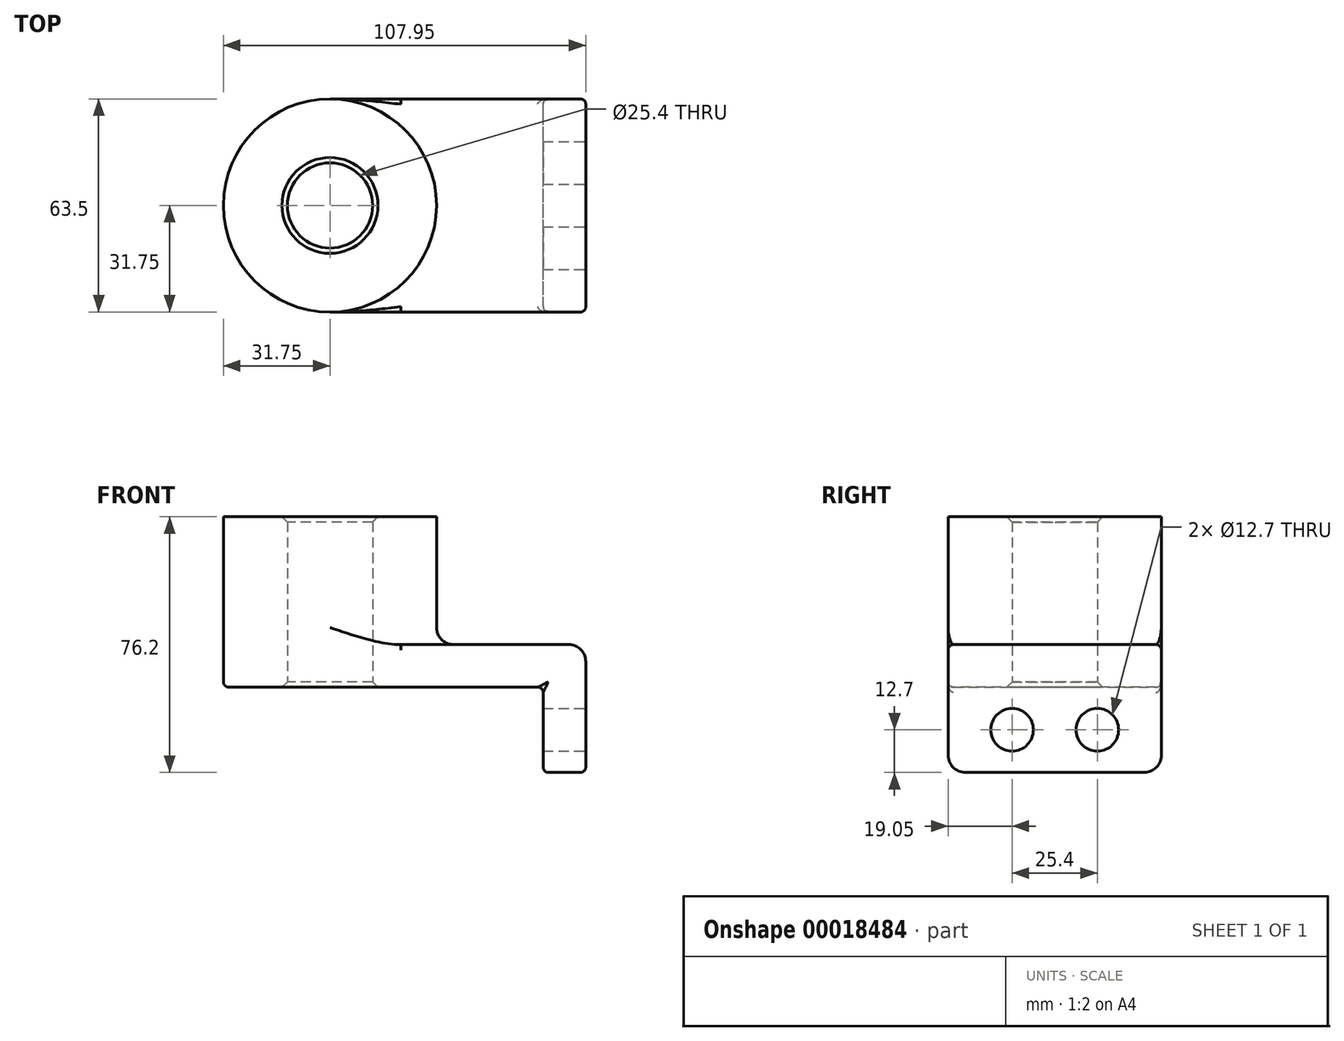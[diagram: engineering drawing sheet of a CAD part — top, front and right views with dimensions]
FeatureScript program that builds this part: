
annotation { "Feature Type Name" : "Feature", "Feature Type Description" : "" }
export const myFeature = defineFeature(function(context is Context, id is Id, definition is map)
    precondition{}
    {
        {
            var Q0;
            Q0=qCreatedBy(makeId("Top.planeOp"),FACE);
            var sketch = newSketch(context, id + "F0", { "sketchPlane" : qUnion([Q0])});
            skLineSegment(sketch, "E0.rect.bottom", {"start": v(38.1, 31.75) * mm, "end": v(-38.1, 31.75) * mm});
            skLineSegment(sketch, "E0.rect.top", {"start": v(38.1, -31.75) * mm, "end": v(-38.1, -31.75) * mm});
            skLineSegment(sketch, "E0.rect.left", {"start": v(38.1, 31.75) * mm, "end": v(38.1, -31.75) * mm});
            skLineSegment(sketch, "E0.rect.right", {"start": v(-38.1, 31.75) * mm, "end": v(-38.1, -31.75) * mm});
            skPoint(sketch, "E0.rect.middle", {"position": v(0, 0) * mm});
            skCircle(sketch, "E1", {"center": v(-38.1, 0) * mm, "radius": 31.75 * mm});
            skCircle(sketch, "E2", {"center": v(-38.1, 0) * mm, "radius": 12.7 * mm});
            skSolve(sketch);
        }
        {
            var Q0;
            {var subQ0=sQuery(id+"F0.wireOp",EDGE,"E2");var subQ1=sQuery(id+"F0.wireOp",EDGE,"E0.rect.right");var subQ3=makeQuery(id+"F0.imprint","INTERSECT",VERTEX,{"disambiguationData":[OD(0.0)],"derivedFrom":[subQ1,subQ0]});Q0=makeQuery(id+"F0.imprint","IMPRINT",FACE,{"disambiguationData":[TD([[makeQuery(id+"F0.imprint","IMPRINT",EDGE,{"disambiguationData":[TD([[subQ3,-1.0]])],"derivedFrom":subQ0}),-1.0]])]});}
            var Q1;
            {var subQ0=sQuery(id+"F0.wireOp",EDGE,"E2");var subQ1=sQuery(id+"F0.wireOp",EDGE,"E0.rect.right");var subQ3=makeQuery(id+"F0.imprint","INTERSECT",VERTEX,{"disambiguationData":[OD(0.0)],"derivedFrom":[subQ1,subQ0]});Q1=makeQuery(id+"F0.imprint","IMPRINT",FACE,{"disambiguationData":[TD([[makeQuery(id+"F0.imprint","IMPRINT",EDGE,{"disambiguationData":[TD([[subQ3,1.0]])],"derivedFrom":subQ0}),-1.0]])]});}
            var Q2;
            {var subQ3=sQuery(id+"F0.wireOp",EDGE,"E0.rect.bottom");Q2=makeQuery(id+"F0.imprint","IMPRINT",FACE,{"disambiguationData":[TD([[makeQuery(id+"F0.imprint","IMPRINT",EDGE,{"derivedFrom":subQ3}),1.0]])]});}
            extrude(context, id + "F1", {"entities" : qUnion([Q0, Q1, Q2]), "depth" : 12.7 * mm});
        }
        {
            var Q0;
            {var subQ0=sQuery(id+"F0.wireOp",EDGE,"E2");var subQ1=sQuery(id+"F0.wireOp",EDGE,"E0.rect.right");var subQ3=makeQuery(id+"F0.imprint","INTERSECT",VERTEX,{"disambiguationData":[OD(0.0)],"derivedFrom":[subQ1,subQ0]});Q0=makeQuery(id+"F0.imprint","IMPRINT",FACE,{"disambiguationData":[TD([[makeQuery(id+"F0.imprint","IMPRINT",EDGE,{"disambiguationData":[TD([[subQ3,-1.0]])],"derivedFrom":subQ0}),-1.0]])]});}
            var Q1;
            {var subQ0=sQuery(id+"F0.wireOp",EDGE,"E2");var subQ1=sQuery(id+"F0.wireOp",EDGE,"E0.rect.right");var subQ3=makeQuery(id+"F0.imprint","INTERSECT",VERTEX,{"disambiguationData":[OD(0.0)],"derivedFrom":[subQ1,subQ0]});Q1=makeQuery(id+"F0.imprint","IMPRINT",FACE,{"disambiguationData":[TD([[makeQuery(id+"F0.imprint","IMPRINT",EDGE,{"disambiguationData":[TD([[subQ3,1.0]])],"derivedFrom":subQ0}),-1.0]])]});}
            extrude(context, id + "F2", {"entities" : qUnion([Q0, Q1]), "flatOperationType" : FlatOperationType.REMOVE, "offsetDistance" : 25.4 * mm, "depth" : 50.8 * mm, "domain" : OperationDomain.MODEL});
        }
        {
            var Q0;
            Q0=makeQuery(id+"F1.opExtrude","SWEPT_FACE",FACE,{"disambiguationData":[OSD([sQuery(id+"F0.wireOp",EDGE,"E0.rect.left")])]});
            var sketch = newSketch(context, id + "F3", { "sketchPlane" : qUnion([Q0])});
            skLineSegment(sketch, "E3.bottom", {"start": v(-31.75, 12.7) * mm, "end": v(31.75, 12.7) * mm});
            skLineSegment(sketch, "E3.top", {"start": v(-31.75, -25.4) * mm, "end": v(31.75, -25.4) * mm});
            skLineSegment(sketch, "E3.left", {"start": v(-31.75, 12.7) * mm, "end": v(-31.75, -25.4) * mm});
            skLineSegment(sketch, "E3.right", {"start": v(31.75, 12.7) * mm, "end": v(31.75, -25.4) * mm});
            skCircle(sketch, "E4", {"center": v(-12.7, -12.7) * mm, "radius": 6.35 * mm});
            skLineSegment(sketch, "E5", {"start": v(0, 0) * mm, "end": v(0, -25.4) * mm});
            skCircle(sketch, "E6.MirrorC", {"center": v(12.7, -12.7) * mm, "radius": 6.35 * mm});
            skSolve(sketch);
        }
        {
            var Q0;
            Q0 = qSketchRegion(id + "F3", true);
            extrude(context, id + "F4", {"entities" : qUnion([Q0]), "operationType" : NewBodyOperationType.ADD, "oppositeDirection" : true, "depth" : 12.7 * mm});
        }
        {
            var Q0;
            Q0=makeQuery(id+"F2.opExtrude","SWEPT_BODY",BODY,{"disambiguationData":[OSD([sQuery(id+"F0.wireOp",EDGE,"E1"),sQuery(id+"F0.wireOp",EDGE,"E2")])]});
            var Q1;
            Q1=makeQuery(id+"F1.opExtrude","SWEPT_BODY",BODY,{"disambiguationData":[OSD([sQuery(id+"F0.wireOp",EDGE,"E0.rect.bottom"),sQuery(id+"F0.wireOp",EDGE,"E0.rect.top"),sQuery(id+"F0.wireOp",EDGE,"E0.rect.left"),sQuery(id+"F0.wireOp",EDGE,"E1"),sQuery(id+"F0.wireOp",EDGE,"E2")])]});
            booleanBodies(context, id + "F5", {"operationType" : BooleanOperationType.UNION, "tools" : qUnion([Q0, Q1])});
        }
        {
            var Q0;
            {var subQ0=sQuery(id+"F0.wireOp",EDGE,"E1");Q0=makeQuery(id+"F5.opBoolean","INTERSECT",EDGE,{"derivedFrom":[makeQuery(id+"F2.opExtrude","SWEPT_FACE",FACE,{"disambiguationData":[OSD([subQ0])]}),makeQuery(id+"F1.opExtrude","CAP_FACE",FACE,{"disambiguationData":[OSD([sQuery(id+"F0.wireOp",EDGE,"E0.rect.bottom"),sQuery(id+"F0.wireOp",EDGE,"E0.rect.top"),sQuery(id+"F0.wireOp",EDGE,"E0.rect.left"),subQ0,sQuery(id+"F0.wireOp",EDGE,"E2")])],"isStart":false})]});}
            fillet(context, id + "F6", {"entities" : qUnion([Q0]), "radius" : 5.08 * mm, "tangentPropagation" : true, "allowEdgeOverflow" : false});
        }
        {
            var Q0;
            Q0=makeQuery(id+"F4.opExtrude","SWEPT_EDGE",EDGE,{"disambiguationData":[OSD([sQuery(id+"F3.wireOp",EDGE,"E3.top"),sQuery(id+"F3.wireOp",EDGE,"E3.left")])]});
            var Q1;
            Q1=makeQuery(id+"F4.opExtrude","SWEPT_EDGE",EDGE,{"disambiguationData":[OSD([sQuery(id+"F3.wireOp",EDGE,"E3.top"),sQuery(id+"F3.wireOp",EDGE,"E3.right")])]});
            fillet(context, id + "F7", {"entities" : qUnion([Q0, Q1]), "radius" : 5.08 * mm, "tangentPropagation" : true, "allowEdgeOverflow" : false});
        }
        {
            var Q0;
            Q0=makeQuery(id+"F1.opExtrude","CAP_EDGE",EDGE,{"disambiguationData":[OSD([sQuery(id+"F0.wireOp",EDGE,"E0.rect.left")])],"isStart":false});
            fillet(context, id + "F8", {"entities" : qUnion([Q0]), "radius" : 5.08 * mm, "tangentPropagation" : true, "allowEdgeOverflow" : false});
        }
        {
            var Q0;
            Q0=makeQuery(id+"F1.opExtrude","CAP_EDGE",EDGE,{"disambiguationData":[OSD([sQuery(id+"F0.wireOp",EDGE,"E0.rect.bottom")])],"isStart":false});
            var Q1;
            {var subQ0=sQuery(id+"F0.wireOp",EDGE,"E1");var subQ1=sQuery(id+"F0.wireOp",EDGE,"E0.rect.bottom");Q1=makeQuery(id+"F6.opFillet","BLEND_EDGE",EDGE,{"blendedFrom":[makeQuery(id+"F5.opBoolean","INTERSECT",EDGE,{"derivedFrom":[makeQuery(id+"F2.opExtrude","SWEPT_FACE",FACE,{"disambiguationData":[OSD([subQ0])]}),makeQuery(id+"F1.opExtrude","CAP_FACE",FACE,{"disambiguationData":[OSD([subQ1,sQuery(id+"F0.wireOp",EDGE,"E0.rect.top"),sQuery(id+"F0.wireOp",EDGE,"E0.rect.left"),subQ0,sQuery(id+"F0.wireOp",EDGE,"E2")])],"isStart":false})]}),makeQuery(id+"F4.boolean.opBoolean","MERGE",FACE,{"derivedFrom":[makeQuery(id+"F1.opExtrude","SWEPT_FACE",FACE,{"disambiguationData":[OSD([subQ1])]}),makeQuery(id+"F4.opExtrude","SWEPT_FACE",FACE,{"disambiguationData":[OSD([sQuery(id+"F3.wireOp",EDGE,"E3.right")])]})]})],"blendedInto":[makeQuery(id+"F4.boolean.opBoolean","MERGE",FACE,{"derivedFrom":[makeQuery(id+"F1.opExtrude","SWEPT_FACE",FACE,{"disambiguationData":[OSD([subQ1])]}),makeQuery(id+"F4.opExtrude","SWEPT_FACE",FACE,{"disambiguationData":[OSD([sQuery(id+"F3.wireOp",EDGE,"E3.right")])]})]})]});}
            fillet(context, id + "F9", {"entities" : qUnion([Q0, Q1]), "radius" : 1.59 * mm, "tangentPropagation" : true, "allowEdgeOverflow" : false});
        }
        {
            var Q0;
            Q0=makeQuery(id+"F4.opExtrude","CAP_EDGE",EDGE,{"disambiguationData":[OSD([sQuery(id+"F3.wireOp",EDGE,"E3.right")])],"isStart":false});
            var Q1;
            Q1=makeQuery(id+"F1.opExtrude","CAP_EDGE",EDGE,{"disambiguationData":[OSD([sQuery(id+"F0.wireOp",EDGE,"E0.rect.bottom")])],"isStart":true});
            fillet(context, id + "F10", {"entities" : qUnion([Q0, Q1]), "radius" : 1.59 * mm, "tangentPropagation" : true, "allowEdgeOverflow" : false});
        }
        {
            var Q0;
            Q0=makeQuery(id+"F4.boolean.opBoolean","INTERSECT",EDGE,{"derivedFrom":[makeQuery(id+"F1.opExtrude","CAP_FACE",FACE,{"disambiguationData":[OSD([sQuery(id+"F0.wireOp",EDGE,"E0.rect.bottom"),sQuery(id+"F0.wireOp",EDGE,"E0.rect.top"),sQuery(id+"F0.wireOp",EDGE,"E0.rect.left"),sQuery(id+"F0.wireOp",EDGE,"E1"),sQuery(id+"F0.wireOp",EDGE,"E2")])],"isStart":true}),makeQuery(id+"F4.opExtrude","CAP_FACE",FACE,{"disambiguationData":[OSD([sQuery(id+"F3.wireOp",EDGE,"E3.bottom"),sQuery(id+"F3.wireOp",EDGE,"E3.top"),sQuery(id+"F3.wireOp",EDGE,"E3.left"),sQuery(id+"F3.wireOp",EDGE,"E3.right"),sQuery(id+"F3.wireOp",EDGE,"E4"),sQuery(id+"F3.wireOp",EDGE,"E6.MirrorC")])],"isStart":false})]});
            fillet(context, id + "F11", {"entities" : qUnion([Q0]), "radius" : 1.59 * mm, "tangentPropagation" : true, "allowEdgeOverflow" : false});
        }
        {
            var Q0;
            Q0=makeQuery(id+"F2.opExtrude","CAP_EDGE",EDGE,{"disambiguationData":[OSD([sQuery(id+"F0.wireOp",EDGE,"E2")])],"isStart":false});
            var Q1;
            Q1=makeQuery(id+"F2.opExtrude","CAP_EDGE",EDGE,{"disambiguationData":[OSD([sQuery(id+"F0.wireOp",EDGE,"E2")])],"isStart":true});
            chamfer(context, id + "F12", {"entities" : qUnion([Q0, Q1]), "width" : 1.59 * mm, "tangentPropagation" : true});
        }
    });
